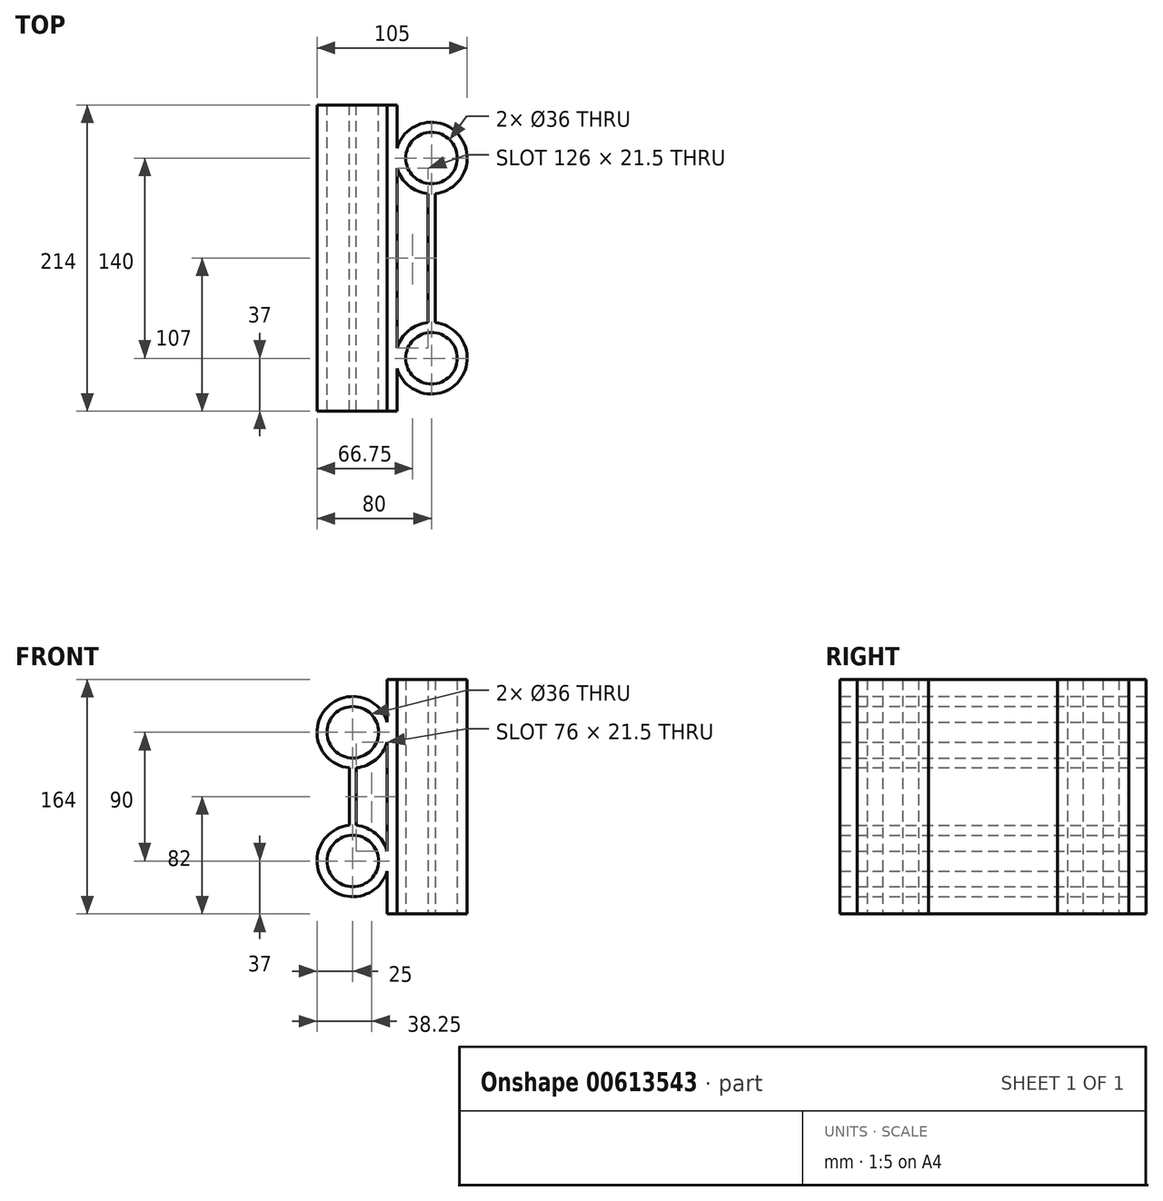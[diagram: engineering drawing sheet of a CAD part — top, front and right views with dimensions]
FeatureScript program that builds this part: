
annotation { "Feature Type Name" : "Feature", "Feature Type Description" : "" }
export const myFeature = defineFeature(function(context is Context, id is Id, definition is map)
    precondition{}
    {
        {
            var Q0;
            Q0=qCreatedBy(makeId("Front.planeOp"),FACE);
            var sketch = newSketch(context, id + "F0", { "sketchPlane" : qUnion([Q0])});
            skCircle(sketch, "E0", {"center": v(-55, 45) * mm, "radius": 18 * mm});
            skCircle(sketch, "E1", {"center": v(-55, -45) * mm, "radius": 18 * mm});
            skCircle(sketch, "E2", {"center": v(-55, 45) * mm, "radius": 25 * mm});
            skCircle(sketch, "E3", {"center": v(-55, -45) * mm, "radius": 25 * mm});
            skLineSegment(sketch, "E4.bottom", {"start": v(-57.5, 20.13) * mm, "end": v(-52.5, 20.13) * mm});
            skLineSegment(sketch, "E4.top", {"start": v(-57.5, -20.13) * mm, "end": v(-52.5, -20.13) * mm});
            skLineSegment(sketch, "E4.left", {"start": v(-57.5, 20.13) * mm, "end": v(-57.5, -20.13) * mm});
            skLineSegment(sketch, "E4.right", {"start": v(-52.5, 20.13) * mm, "end": v(-52.5, -20.13) * mm});
            skLineSegment(sketch, "E5", {"start": v(-55, 20.13) * mm, "end": v(-55, 45) * mm, "construction": true});
            skSolve(sketch);
        }
        {
            var Q0;
            Q0=qCreatedBy(makeId("Top.planeOp"),FACE);
            var sketch = newSketch(context, id + "F1", { "sketchPlane" : qUnion([Q0])});
            skCircle(sketch, "E6", {"center": v(0, 70) * mm, "radius": 18 * mm});
            skCircle(sketch, "E7", {"center": v(0, -70) * mm, "radius": 18 * mm});
            skCircle(sketch, "E8", {"center": v(0, 70) * mm, "radius": 25 * mm});
            skCircle(sketch, "E9", {"center": v(0, -70) * mm, "radius": 25 * mm});
            skLineSegment(sketch, "E10.bottom", {"start": v(-2.5, 45.13) * mm, "end": v(2.5, 45.13) * mm});
            skLineSegment(sketch, "E10.top", {"start": v(-2.5, -45.13) * mm, "end": v(2.5, -45.13) * mm});
            skLineSegment(sketch, "E10.left", {"start": v(-2.5, 45.13) * mm, "end": v(-2.5, -45.13) * mm});
            skLineSegment(sketch, "E10.right", {"start": v(2.5, 45.13) * mm, "end": v(2.5, -45.13) * mm});
            skLineSegment(sketch, "E11", {"start": v(0, 45.13) * mm, "end": v(0, 70) * mm, "construction": true});
            skSolve(sketch);
        }
        {
            var Q0;
            Q0=qCreatedBy(makeId("Top.planeOp"),FACE);
            var sketch = newSketch(context, id + "F2", { "sketchPlane" : qUnion([Q0])});
            skLineSegment(sketch, "E12.bottom", {"start": v(-31, 107) * mm, "end": v(-24, 107) * mm});
            skLineSegment(sketch, "E12.top", {"start": v(-31, -107) * mm, "end": v(-24, -107) * mm});
            skLineSegment(sketch, "E12.left", {"start": v(-31, 107) * mm, "end": v(-31, -107) * mm});
            skLineSegment(sketch, "E12.right", {"start": v(-24, 107) * mm, "end": v(-24, -107) * mm});
            skSolve(sketch);
        }
        {
            var Q0;
            Q0=makeQuery(id+"F2.imprint","IMPRINT",FACE,{"disambiguationData":[TD([[makeQuery(id+"F2.imprint","IMPRINT",EDGE,{"derivedFrom":sQuery(id+"F2.wireOp",EDGE,"E12.bottom")}),-1.0]])]});
            extrude(context, id + "F3", {"entities" : qUnion([Q0]), "depth" : 82 * mm, "offsetDistance" : 25 * mm, "hasSecondDirection" : true, "secondDirectionOppositeDirection" : true, "secondDirectionDepth" : 82 * mm});
        }
        {
            var Q0;
            Q0=makeQuery(id+"F0.imprint","IMPRINT",FACE,{"disambiguationData":[TD([[makeQuery(id+"F0.imprint","IMPRINT",EDGE,{"derivedFrom":sQuery(id+"F0.wireOp",EDGE,"E0")}),-1.0]])]});
            var Q1;
            Q1=makeQuery(id+"F0.imprint","IMPRINT",FACE,{"disambiguationData":[TD([[makeQuery(id+"F0.imprint","IMPRINT",EDGE,{"derivedFrom":sQuery(id+"F0.wireOp",EDGE,"E1")}),-1.0]])]});
            var Q2;
            {var subQ0=sQuery(id+"F0.wireOp",EDGE,"E4.bottom");Q2=makeQuery(id+"F0.imprint","IMPRINT",FACE,{"disambiguationData":[TD([[makeQuery(id+"F0.imprint","IMPRINT",EDGE,{"derivedFrom":subQ0}),-1.0]])]});}
            var Q3;
            {var subQ0=sQuery(id+"F0.wireOp",EDGE,"E4.left");Q3=makeQuery(id+"F0.imprint","IMPRINT",FACE,{"disambiguationData":[TD([[makeQuery(id+"F0.imprint","IMPRINT",EDGE,{"derivedFrom":subQ0}),1.0]])]});}
            var Q4;
            {var subQ0=sQuery(id+"F0.wireOp",EDGE,"E4.top");Q4=makeQuery(id+"F0.imprint","IMPRINT",FACE,{"disambiguationData":[TD([[makeQuery(id+"F0.imprint","IMPRINT",EDGE,{"derivedFrom":subQ0}),1.0]])]});}
            extrude(context, id + "F4", {"entities" : qUnion([Q0, Q1, Q2, Q3, Q4]), "operationType" : NewBodyOperationType.ADD, "depth" : 107 * mm, "offsetDistance" : 25 * mm, "hasSecondDirection" : true, "secondDirectionOppositeDirection" : true, "secondDirectionDepth" : 107 * mm});
        }
        {
            var Q0;
            Q0=makeQuery(id+"F1.imprint","IMPRINT",FACE,{"disambiguationData":[TD([[makeQuery(id+"F1.imprint","IMPRINT",EDGE,{"derivedFrom":sQuery(id+"F1.wireOp",EDGE,"E6")}),-1.0]])]});
            var Q1;
            {var subQ0=sQuery(id+"F1.wireOp",EDGE,"E10.left");Q1=makeQuery(id+"F1.imprint","IMPRINT",FACE,{"disambiguationData":[TD([[makeQuery(id+"F1.imprint","IMPRINT",EDGE,{"derivedFrom":subQ0}),1.0]])]});}
            var Q2;
            {var subQ0=sQuery(id+"F1.wireOp",EDGE,"E10.bottom");Q2=makeQuery(id+"F1.imprint","IMPRINT",FACE,{"disambiguationData":[TD([[makeQuery(id+"F1.imprint","IMPRINT",EDGE,{"derivedFrom":subQ0}),-1.0]])]});}
            var Q3;
            Q3=makeQuery(id+"F1.imprint","IMPRINT",FACE,{"disambiguationData":[TD([[makeQuery(id+"F1.imprint","IMPRINT",EDGE,{"derivedFrom":sQuery(id+"F1.wireOp",EDGE,"E7")}),-1.0]])]});
            var Q4;
            {var subQ0=sQuery(id+"F1.wireOp",EDGE,"E10.top");Q4=makeQuery(id+"F1.imprint","IMPRINT",FACE,{"disambiguationData":[TD([[makeQuery(id+"F1.imprint","IMPRINT",EDGE,{"derivedFrom":subQ0}),1.0]])]});}
            extrude(context, id + "F5", {"entities" : qUnion([Q0, Q1, Q2, Q3, Q4]), "operationType" : NewBodyOperationType.ADD, "depth" : 82 * mm, "offsetDistance" : 25 * mm, "hasSecondDirection" : true, "secondDirectionOppositeDirection" : true, "secondDirectionDepth" : 82 * mm});
        }
    });
